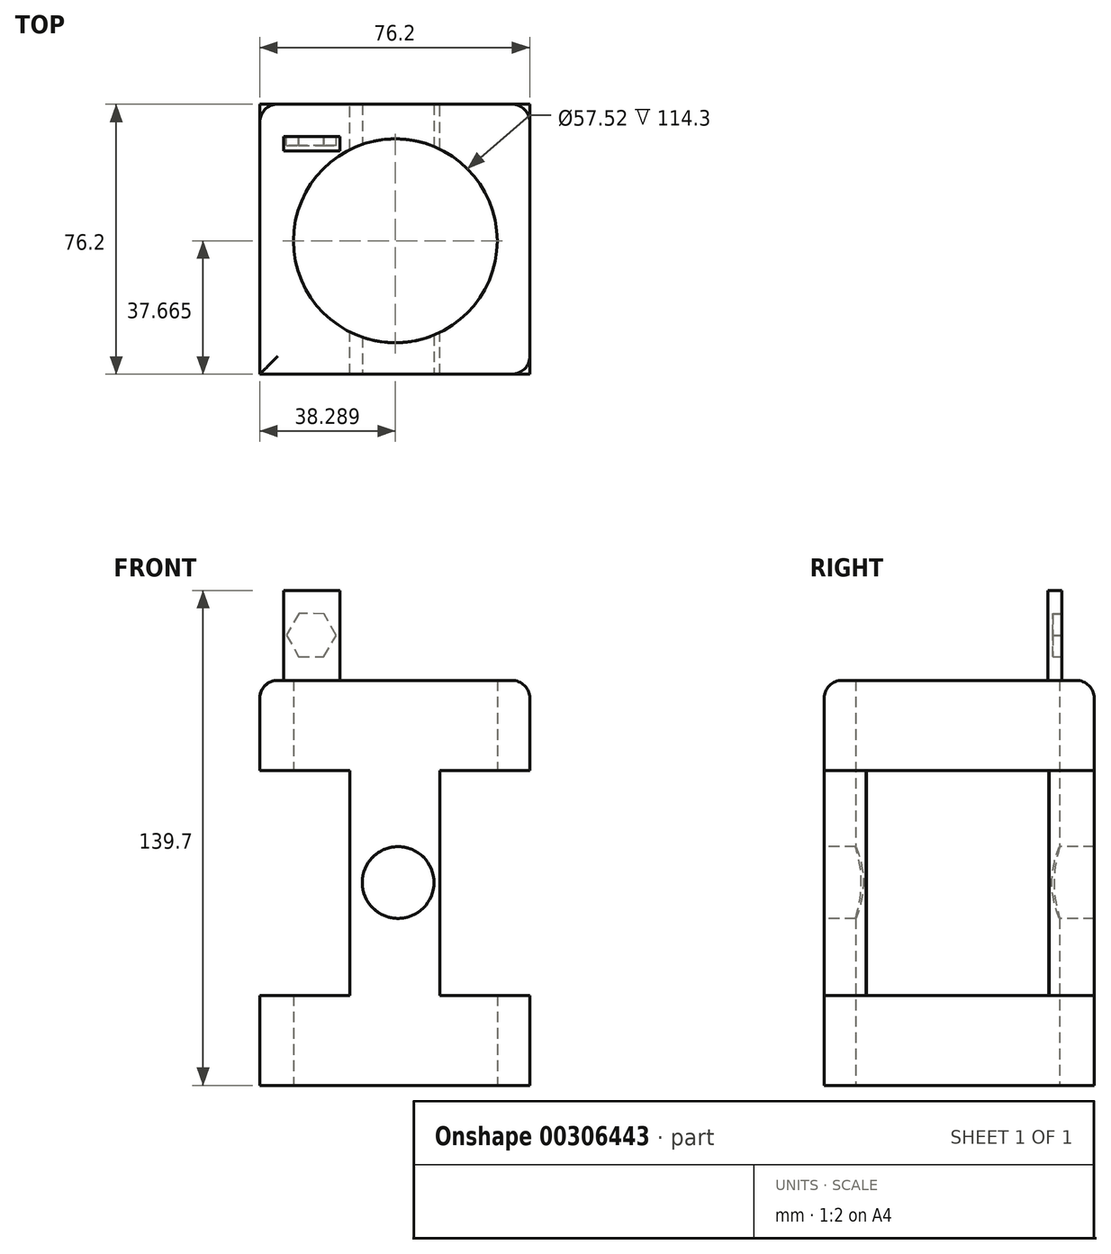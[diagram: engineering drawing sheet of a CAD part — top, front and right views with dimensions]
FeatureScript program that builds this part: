
annotation { "Feature Type Name" : "Feature", "Feature Type Description" : "" }
export const myFeature = defineFeature(function(context is Context, id is Id, definition is map)
    precondition{}
    {
        {
            var Q0;
            Q0=qCreatedBy(makeId("Front.planeOp"),FACE);
            var sketch = newSketch(context, id + "F0", { "sketchPlane" : qUnion([Q0])});
            skLineSegment(sketch, "E0", {"start": v(-44.17, -53.06) * mm, "end": v(32.03, -53.06) * mm});
            skLineSegment(sketch, "E1", {"start": v(32.03, -53.06) * mm, "end": v(32.03, -27.66) * mm});
            skLineSegment(sketch, "E2", {"start": v(32.03, -27.66) * mm, "end": v(6.63, -27.66) * mm});
            skLineSegment(sketch, "E3", {"start": v(6.63, -27.66) * mm, "end": v(6.63, 35.84) * mm});
            skLineSegment(sketch, "E4", {"start": v(6.63, 35.84) * mm, "end": v(32.03, 35.84) * mm});
            skLineSegment(sketch, "E5", {"start": v(32.03, 35.84) * mm, "end": v(32.03, 61.24) * mm});
            skLineSegment(sketch, "E6", {"start": v(32.03, 61.24) * mm, "end": v(-44.17, 61.24) * mm});
            skLineSegment(sketch, "E7", {"start": v(-44.17, 61.24) * mm, "end": v(-44.17, 35.84) * mm});
            skLineSegment(sketch, "E8", {"start": v(-44.17, 35.84) * mm, "end": v(-18.77, 35.84) * mm});
            skLineSegment(sketch, "E9", {"start": v(-18.77, 35.84) * mm, "end": v(-18.77, -27.66) * mm});
            skLineSegment(sketch, "E10", {"start": v(-18.77, -27.66) * mm, "end": v(-44.17, -27.66) * mm});
            skLineSegment(sketch, "E11", {"start": v(-44.17, -27.66) * mm, "end": v(-44.17, -53.06) * mm});
            skSolve(sketch);
        }
        {
            var Q0;
            Q0=makeQuery(id+"F0.imprint","IMPRINT",FACE,{"disambiguationData":[TD([[makeQuery(id+"F0.imprint","IMPRINT",EDGE,{"derivedFrom":sQuery(id+"F0.wireOp",EDGE,"E0")}),1.0]])]});
            extrude(context, id + "F1", {"entities" : qUnion([Q0]), "depth" : 76.2 * mm});
        }
        {
            var Q0;
            Q0=makeQuery(id+"F1.opExtrude","SWEPT_FACE",FACE,{"disambiguationData":[OSD([sQuery(id+"F0.wireOp",EDGE,"E3")])]});
            var sketch = newSketch(context, id + "F2", { "sketchPlane" : qUnion([Q0])});
            skCircle(sketch, "E12", {"center": v(-43.02, 3.56) * mm, "radius": 16.76 * mm});
            skSolve(sketch);
        }
        {
            var Q0;
            Q0=makeQuery(id+"F2.imprint","IMPRINT",FACE,{"disambiguationData":[TD([[makeQuery(id+"F2.imprint","IMPRINT",EDGE,{"derivedFrom":sQuery(id+"F2.wireOp",EDGE,"E12")}),1.0]])]});
            extrude(context, id + "F3", {"entities" : qUnion([Q0]), "operationType" : NewBodyOperationType.REMOVE, "endBound" : BoundingType.THROUGH_ALL, "oppositeDirection" : true, "depth" : 25.4 * mm});
        }
        {
            var Q0;
            Q0=makeQuery(id+"F1.opExtrude","CAP_FACE",FACE,{"disambiguationData":[OSD([sQuery(id+"F0.wireOp",EDGE,"E0"),sQuery(id+"F0.wireOp",EDGE,"E1"),sQuery(id+"F0.wireOp",EDGE,"E2"),sQuery(id+"F0.wireOp",EDGE,"E3"),sQuery(id+"F0.wireOp",EDGE,"E4"),sQuery(id+"F0.wireOp",EDGE,"E5"),sQuery(id+"F0.wireOp",EDGE,"E6"),sQuery(id+"F0.wireOp",EDGE,"E7"),sQuery(id+"F0.wireOp",EDGE,"E8"),sQuery(id+"F0.wireOp",EDGE,"E9"),sQuery(id+"F0.wireOp",EDGE,"E10"),sQuery(id+"F0.wireOp",EDGE,"E11")])],"isStart":false});
            var sketch = newSketch(context, id + "F4", { "sketchPlane" : qUnion([Q0])});
            skCircle(sketch, "E13", {"center": v(-5.12, 4.19) * mm, "radius": 10.12 * mm});
            skSolve(sketch);
        }
        {
            var Q0;
            Q0=makeQuery(id+"F4.imprint","IMPRINT",FACE,{"disambiguationData":[TD([[makeQuery(id+"F4.imprint","IMPRINT",EDGE,{"derivedFrom":sQuery(id+"F4.wireOp",EDGE,"E13")}),1.0]])]});
            extrude(context, id + "F5", {"entities" : qUnion([Q0]), "operationType" : NewBodyOperationType.REMOVE, "endBound" : BoundingType.THROUGH_ALL, "oppositeDirection" : true, "depth" : 25.4 * mm});
        }
        {
            var Q0;
            Q0=makeQuery(id+"F1.opExtrude","SWEPT_FACE",FACE,{"disambiguationData":[OSD([sQuery(id+"F0.wireOp",EDGE,"E0")])]});
            var sketch = newSketch(context, id + "F6", { "sketchPlane" : qUnion([Q0])});
            skCircle(sketch, "E14", {"center": v(-5.88, 38.53) * mm, "radius": 28.76 * mm});
            skSolve(sketch);
        }
        {
            var Q0;
            Q0=makeQuery(id+"F6.imprint","IMPRINT",FACE,{"disambiguationData":[TD([[makeQuery(id+"F6.imprint","IMPRINT",EDGE,{"derivedFrom":sQuery(id+"F6.wireOp",EDGE,"E14")}),1.0]])]});
            extrude(context, id + "F7", {"entities" : qUnion([Q0]), "operationType" : NewBodyOperationType.REMOVE, "endBound" : BoundingType.THROUGH_ALL, "oppositeDirection" : true, "depth" : 25.4 * mm});
        }
        {
            var Q0;
            Q0=makeQuery(id+"F1.opExtrude","CAP_EDGE",EDGE,{"disambiguationData":[OSD([sQuery(id+"F0.wireOp",EDGE,"E6")])],"isStart":false});
            var Q1;
            Q1=makeQuery(id+"F1.opExtrude","SWEPT_EDGE",EDGE,{"disambiguationData":[OSD([sQuery(id+"F0.wireOp",EDGE,"E5"),sQuery(id+"F0.wireOp",EDGE,"E6")])]});
            var Q2;
            Q2=makeQuery(id+"F1.opExtrude","CAP_EDGE",EDGE,{"disambiguationData":[OSD([sQuery(id+"F0.wireOp",EDGE,"E5")])],"isStart":false});
            var Q3;
            Q3=makeQuery(id+"F1.opExtrude","CAP_EDGE",EDGE,{"disambiguationData":[OSD([sQuery(id+"F0.wireOp",EDGE,"E6")])],"isStart":true});
            var Q4;
            Q4=makeQuery(id+"F1.opExtrude","CAP_EDGE",EDGE,{"disambiguationData":[OSD([sQuery(id+"F0.wireOp",EDGE,"E5")])],"isStart":true});
            var Q5;
            Q5=makeQuery(id+"F1.opExtrude","CAP_EDGE",EDGE,{"disambiguationData":[OSD([sQuery(id+"F0.wireOp",EDGE,"E7")])],"isStart":true});
            var Q6;
            Q6=makeQuery(id+"F1.opExtrude","SWEPT_EDGE",EDGE,{"disambiguationData":[OSD([sQuery(id+"F0.wireOp",EDGE,"E6"),sQuery(id+"F0.wireOp",EDGE,"E7")])]});
            fillet(context, id + "F8", {"entities" : qUnion([Q0, Q1, Q2, Q3, Q4, Q5, Q6]), "radius" : 5.08 * mm, "tangentPropagation" : true, "allowEdgeOverflow" : false});
        }
        {
            var Q0;
            Q0=makeQuery(id+"F1.opExtrude","SWEPT_FACE",FACE,{"disambiguationData":[OSD([sQuery(id+"F0.wireOp",EDGE,"E6")])]});
            var sketch = newSketch(context, id + "F9", { "sketchPlane" : qUnion([Q0])});
            skSolve(sketch);
        }
        {
            var Q0;
            {var subQ0=sQuery(id+"F0.wireOp",EDGE,"E6");var subQ1=makeQuery(id+"F1.opExtrude","SWEPT_FACE",FACE,{"disambiguationData":[OSD([subQ0])]});Q0=makeQuery(id+"F9.imprint","IMPRINT",FACE,{"disambiguationData":[TD([[makeQuery(id+"F9.imprint","IMPRINT",EDGE,{"derivedFrom":makeQuery(id+"F7.boolean.opBoolean","INTERSECT",EDGE,{"derivedFrom":[subQ1,makeQuery(id+"F7.opExtrude","SWEPT_FACE",FACE,{"disambiguationData":[OSD([sQuery(id+"F6.wireOp",EDGE,"E14")])]})]})}),1.0]])]});}
            var sketch = newSketch(context, id + "F10", { "sketchPlane" : qUnion([Q0])});
            skLineSegment(sketch, "E15.bottom", {"start": v(-21.54, -9.16) * mm, "end": v(-37.42, -9.16) * mm});
            skLineSegment(sketch, "E15.top", {"start": v(-21.54, -13.13) * mm, "end": v(-37.42, -13.13) * mm});
            skLineSegment(sketch, "E15.left", {"start": v(-21.54, -9.16) * mm, "end": v(-21.54, -13.13) * mm});
            skLineSegment(sketch, "E15.right", {"start": v(-37.42, -9.16) * mm, "end": v(-37.42, -13.13) * mm});
            skSolve(sketch);
        }
        {
            var Q0;
            Q0=makeQuery(id+"F10.imprint","IMPRINT",FACE,{"disambiguationData":[TD([[makeQuery(id+"F10.imprint","IMPRINT",EDGE,{"derivedFrom":sQuery(id+"F10.wireOp",EDGE,"E15.bottom")}),1.0]])]});
            extrude(context, id + "F11", {"entities" : qUnion([Q0]), "operationType" : NewBodyOperationType.ADD, "depth" : 25.4 * mm});
        }
        {
            var Q0;
            Q0=makeQuery(id+"F11.opExtrude","SWEPT_FACE",FACE,{"disambiguationData":[OSD([sQuery(id+"F10.wireOp",EDGE,"E15.bottom")])]});
            var sketch = newSketch(context, id + "F12", { "sketchPlane" : qUnion([Q0])});
            skCircle(sketch, "E16.cCircle", {"center": v(29.6, 74) * mm, "radius": 6.07 * mm, "construction": true});
            skLineSegment(sketch, "E16.0", {"start": v(36.61, 74.07) * mm, "end": v(33.16, 67.96) * mm});
            skLineSegment(sketch, "E16.1", {"start": v(33.16, 67.96) * mm, "end": v(26.15, 67.9) * mm});
            skLineSegment(sketch, "E16.2", {"start": v(26.15, 67.9) * mm, "end": v(22.59, 73.94) * mm});
            skLineSegment(sketch, "E16.3", {"start": v(22.59, 73.94) * mm, "end": v(26.04, 80.04) * mm});
            skLineSegment(sketch, "E16.4", {"start": v(26.04, 80.04) * mm, "end": v(33.05, 80.1) * mm});
            skLineSegment(sketch, "E16.5", {"start": v(33.05, 80.1) * mm, "end": v(36.61, 74.07) * mm});
            skPoint(sketch, "E16.0.midPoint", {"position": v(34.89, 71.01) * mm});
            skSolve(sketch);
        }
        {
            var Q0;
            Q0=makeQuery(id+"F12.imprint","IMPRINT",FACE,{"disambiguationData":[TD([[makeQuery(id+"F12.imprint","IMPRINT",EDGE,{"derivedFrom":sQuery(id+"F12.wireOp",EDGE,"E16.0")}),-1.0]])]});
            extrude(context, id + "F13", {"entities" : qUnion([Q0]), "operationType" : NewBodyOperationType.REMOVE, "oppositeDirection" : true, "depth" : 2.54 * mm});
        }
    });
